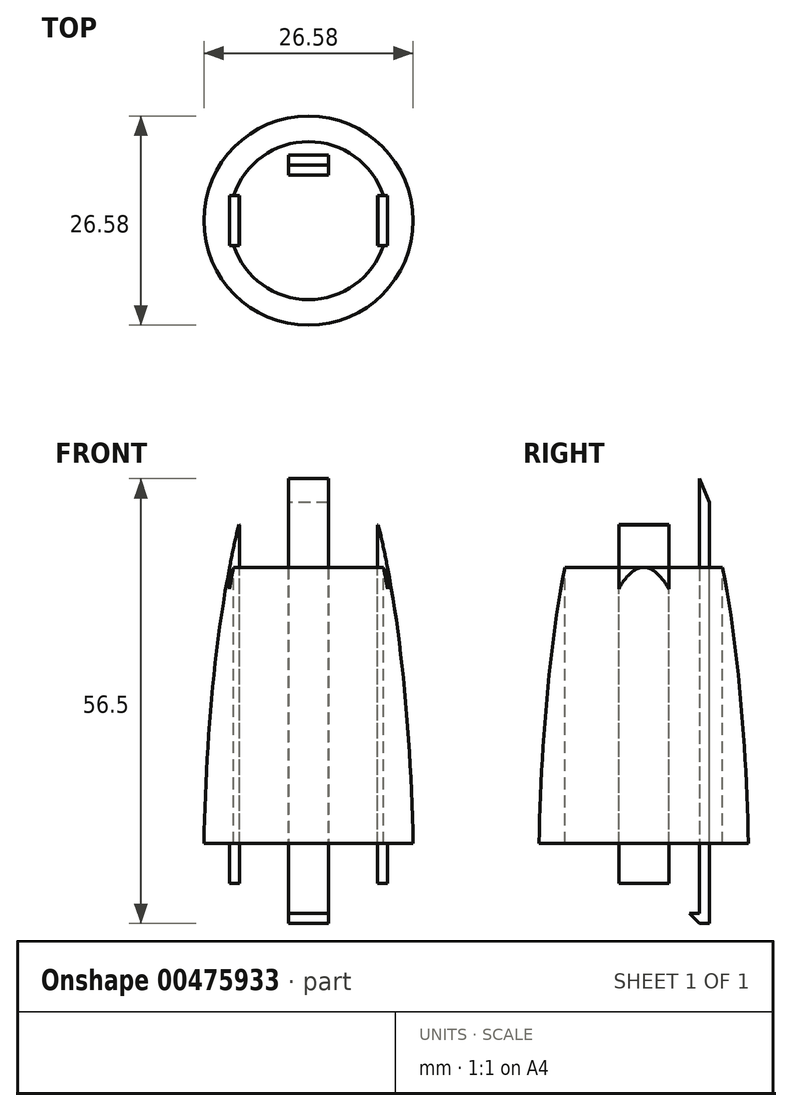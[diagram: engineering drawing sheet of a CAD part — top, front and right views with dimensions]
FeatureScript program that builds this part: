
annotation { "Feature Type Name" : "Feature", "Feature Type Description" : "" }
export const myFeature = defineFeature(function(context is Context, id is Id, definition is map)
    precondition{}
    {
        {
            var Q0;
            Q0=qCreatedBy(makeId("Front.planeOp"),FACE);
            var sketch = newSketch(context, id + "F0", { "sketchPlane" : qUnion([Q0])});
            skEllipticalArc(sketch, "E0", {});
            skLineSegment(sketch, "E1", {"start": v(0, 63.5) * mm, "end": v(0, 52.07) * mm});
            skLineSegment(sketch, "E2", {"start": v(4.44, 0) * mm, "end": v(15.88, 0) * mm});
            skPoint(sketch, "E3.orphan", {"position": v(-15.88, 0) * mm});
            skLineSegment(sketch, "E4", {"start": v(15.88, 0) * mm, "end": v(13.34, 0) * mm, "construction": true});
            skLineSegment(sketch, "E5", {"start": v(0, 0) * mm, "end": v(8.76, 0) * mm});
            skLineSegment(sketch, "E6", {"start": v(8.76, 0) * mm, "end": v(8.76, 41.66) * mm});
            skLineSegment(sketch, "E7", {"start": v(8.76, 41.66) * mm, "end": v(8.76, 43.42) * mm});
            skLineSegment(sketch, "E8", {"start": v(8.76, 43.42) * mm, "end": v(8.76, 44.92) * mm});
            skLineSegment(sketch, "E9", {"start": v(8.76, 44.92) * mm, "end": v(8.76, 45.57) * mm});
            skLineSegment(sketch, "E10", {"start": v(0, 60.96) * mm, "end": v(0, 0) * mm, "construction": true});
            skLineSegment(sketch, "E11.MirrorCS", {"start": v(-8.76, 0) * mm, "end": v(-8.76, 41.66) * mm});
            skLineSegment(sketch, "E12.MirrorCS", {"start": v(-8.76, 41.66) * mm, "end": v(-8.76, 43.42) * mm});
            skLineSegment(sketch, "E13.MirrorCS", {"start": v(-8.76, 43.42) * mm, "end": v(-8.76, 44.92) * mm});
            skLineSegment(sketch, "E14.MirrorCS", {"start": v(-8.76, 44.92) * mm, "end": v(-8.76, 45.57) * mm});
            skLineSegment(sketch, "E15.bottom", {"start": v(8.76, 45.57) * mm, "end": v(8.86, 45.57) * mm});
            skLineSegment(sketch, "E15.top", {"start": v(8.76, 0) * mm, "end": v(10.03, 0) * mm});
            skLineSegment(sketch, "E15.left", {"start": v(8.76, 45.57) * mm, "end": v(8.76, 0) * mm});
            skLineSegment(sketch, "E15.right", {"start": v(10.03, 40.16) * mm, "end": v(10.03, 0) * mm});
            skLineSegment(sketch, "E16.MirrorCS", {"start": v(-8.76, 0) * mm, "end": v(-10.03, 0) * mm});
            skPoint(sketch, "E17.orphan", {"position": v(10.03, 45.57) * mm});
            skPoint(sketch, "E18.MirrorCS.end.orphan", {"position": v(-10.03, 45.57) * mm});
            skPoint(sketch, "E18.MirrorCS.start.orphan", {"position": v(-8.76, 45.57) * mm});
            skPoint(sketch, "E19.MirrorCS.end.orphan", {"position": v(-10.03, 0) * mm});
            skLineSegment(sketch, "E20.MirrorCS", {"start": v(-10.03, 40.16) * mm, "end": v(-10.03, 0) * mm});
            skEllipticalArc(sketch, "E21.MirrorCS", {});
            skPoint(sketch, "E22.orphan", {"position": v(-13.34, 0) * mm});
            skLineSegment(sketch, "E23", {"start": v(-8.76, 45.57) * mm, "end": v(-8.84, 45.62) * mm});
            const initialGuessF0  = {"E0": [0, 0, 0, 1, 0.0635, 0.015875, 4.71238898038469, 0], "E0": [0, 0, 0, 1, 0.06096, 0.013335, 4.71238898038469, 0], "E21.MirrorCS": [0, 0, 0, 1, 0.06096, 0.013335, 0, 0.8516691248618306]};
            skSetInitialGuess(sketch, initialGuessF0);
            skSolve(sketch);
        }
        {
            var Q0;
            {var subQ7=sQuery(id+"F0.wireOp",EDGE,"E0");Q0=makeQuery(id+"F0.imprint","IMPRINT",FACE,{"disambiguationData":[TD([[makeQuery(id+"F0.imprint","IMPRINT",EDGE,{"derivedFrom":subQ7}),1.0]])]});}
            var Q1;
            Q1=sQuery(id+"F0.wireOp",EDGE,"E1");
            revolve(context, id + "F1", {"entities" : qUnion([Q0]), "axis" : qUnion([Q1]), "revolveType" : RevolveType.FULL});
        }
        {
            var Q0;
            Q0=makeQuery(id+"F1.opRevolve","SWEPT_FACE",FACE,{"disambiguationData":[OSD([sQuery(id+"F0.wireOp",EDGE,"E2")])]});
            var sketch = newSketch(context, id + "F2", { "sketchPlane" : qUnion([Q0])});
            skCircle(sketch, "E24.0", {"center": v(0, 0) * mm, "radius": 14.44 * mm});
            skSolve(sketch);
        }
        {
            var Q0;
            Q0 = qSketchRegion(id + "F2", true);
            extrude(context, id + "F3", {"entities" : qUnion([Q0]), "operationType" : NewBodyOperationType.REMOVE, "oppositeDirection" : true, "depth" : 5.08 * mm, "offsetDistance" : 25.4 * mm});
        }
        {
            var Q0;
            Q0=makeQuery(id+"F0.imprint","IMPRINT",FACE,{"disambiguationData":[TD([[makeQuery(id+"F0.imprint","IMPRINT",EDGE,{"derivedFrom":sQuery(id+"F0.wireOp",EDGE,"E11.MirrorCS")}),1.0]])]});
            var Q1;
            {var subQ0=sQuery(id+"F0.wireOp",EDGE,"E15.bottom");Q1=makeQuery(id+"F0.imprint","IMPRINT",FACE,{"disambiguationData":[TD([[makeQuery(id+"F0.imprint","IMPRINT",EDGE,{"derivedFrom":subQ0}),-1.0]])]});}
            extrude(context, id + "F4", {"entities" : qUnion([Q0, Q1]), "operationType" : NewBodyOperationType.ADD, "endBound" : BoundingType.SYMMETRIC, "depth" : 6.35 * mm, "offsetDistance" : 25.4 * mm});
        }
        {
            var Q0;
            Q0=qCreatedBy(makeId("Right.planeOp"),FACE);
            var sketch = newSketch(context, id + "F5", { "sketchPlane" : qUnion([Q0])});
            skLineSegment(sketch, "E25.0", {"start": v(-14.44, 0) * mm, "end": v(14.44, 0) * mm});
            skLineSegment(sketch, "E26.bottom", {"start": v(7.06, 51.42) * mm, "end": v(-7.06, 51.42) * mm});
            skLineSegment(sketch, "E26.left", {"start": v(7.06, 51.42) * mm, "end": v(7.06, 0) * mm});
            skLineSegment(sketch, "E26.right", {"start": v(-7.06, 51.42) * mm, "end": v(-7.06, 0) * mm});
            skPoint(sketch, "E26.middle", {"position": v(0, 0) * mm});
            skLineSegment(sketch, "E27", {"start": v(-7.06, 0) * mm, "end": v(-8.33, 0) * mm});
            skLineSegment(sketch, "E28", {"start": v(-8.33, 0) * mm, "end": v(-8.33, 48.42) * mm});
            skLineSegment(sketch, "E29", {"start": v(-8.33, 48.42) * mm, "end": v(-7.06, 51.42) * mm});
            skLineSegment(sketch, "E30.MirrorCS", {"start": v(8.33, 0) * mm, "end": v(8.33, 48.42) * mm});
            skLineSegment(sketch, "E31.MirrorCS", {"start": v(8.33, 48.42) * mm, "end": v(7.06, 51.42) * mm});
            skLineSegment(sketch, "E32", {"start": v(7.06, 0) * mm, "end": v(7.06, -5.08) * mm});
            skLineSegment(sketch, "E33", {"start": v(7.06, -5.08) * mm, "end": v(8.33, -5.08) * mm});
            skLineSegment(sketch, "E34", {"start": v(8.33, -5.08) * mm, "end": v(8.33, 0) * mm});
            skLineSegment(sketch, "E35", {"start": v(-8.33, 0) * mm, "end": v(-8.33, -5.08) * mm});
            skLineSegment(sketch, "E36", {"start": v(-8.33, -5.08) * mm, "end": v(-7.06, -5.08) * mm});
            skLineSegment(sketch, "E37", {"start": v(-7.06, -5.08) * mm, "end": v(-7.06, 0) * mm});
            skLineSegment(sketch, "E38.top", {"start": v(7.06, -3.81) * mm, "end": v(5.8, -3.81) * mm});
            skLineSegment(sketch, "E38.left", {"start": v(7.06, -5.08) * mm, "end": v(7.06, -3.81) * mm});
            skLineSegment(sketch, "E39", {"start": v(5.8, -3.81) * mm, "end": v(7.06, -5.08) * mm});
            skSolve(sketch);
        }
        {
            var Q0;
            {var subQ2=sQuery(id+"F5.wireOp",EDGE,"E27");Q0=makeQuery(id+"F5.imprint","IMPRINT",FACE,{"disambiguationData":[TD([[makeQuery(id+"F5.imprint","IMPRINT",EDGE,{"derivedFrom":subQ2}),-1.0]])]});}
            var Q1;
            {var subQ0=sQuery(id+"F5.wireOp",EDGE,"E30.MirrorCS");Q1=makeQuery(id+"F5.imprint","IMPRINT",FACE,{"disambiguationData":[TD([[makeQuery(id+"F5.imprint","IMPRINT",EDGE,{"derivedFrom":subQ0}),1.0]])]});}
            var Q2;
            {var subQ0=sQuery(id+"F5.wireOp",EDGE,"E32");Q2=makeQuery(id+"F5.imprint","IMPRINT",FACE,{"disambiguationData":[TD([[makeQuery(id+"F5.imprint","IMPRINT",EDGE,{"derivedFrom":subQ0}),1.0]])]});}
            var Q3;
            Q3=makeQuery(id+"F5.imprint","IMPRINT",FACE,{"disambiguationData":[TD([[makeQuery(id+"F5.imprint","IMPRINT",EDGE,{"derivedFrom":sQuery(id+"F5.wireOp",EDGE,"E27")}),1.0]])]});
            var Q4;
            Q4=makeQuery(id+"F5.imprint","IMPRINT",FACE,{"disambiguationData":[TD([[makeQuery(id+"F5.imprint","IMPRINT",EDGE,{"derivedFrom":sQuery(id+"F5.wireOp",EDGE,"E38.top")}),1.0]])]});
            extrude(context, id + "F6", {"entities" : qUnion([Q0, Q1, Q2, Q3, Q4]), "operationType" : NewBodyOperationType.ADD, "endBound" : BoundingType.SYMMETRIC, "depth" : 5.08 * mm, "offsetDistance" : 25.4 * mm});
        }
    });
